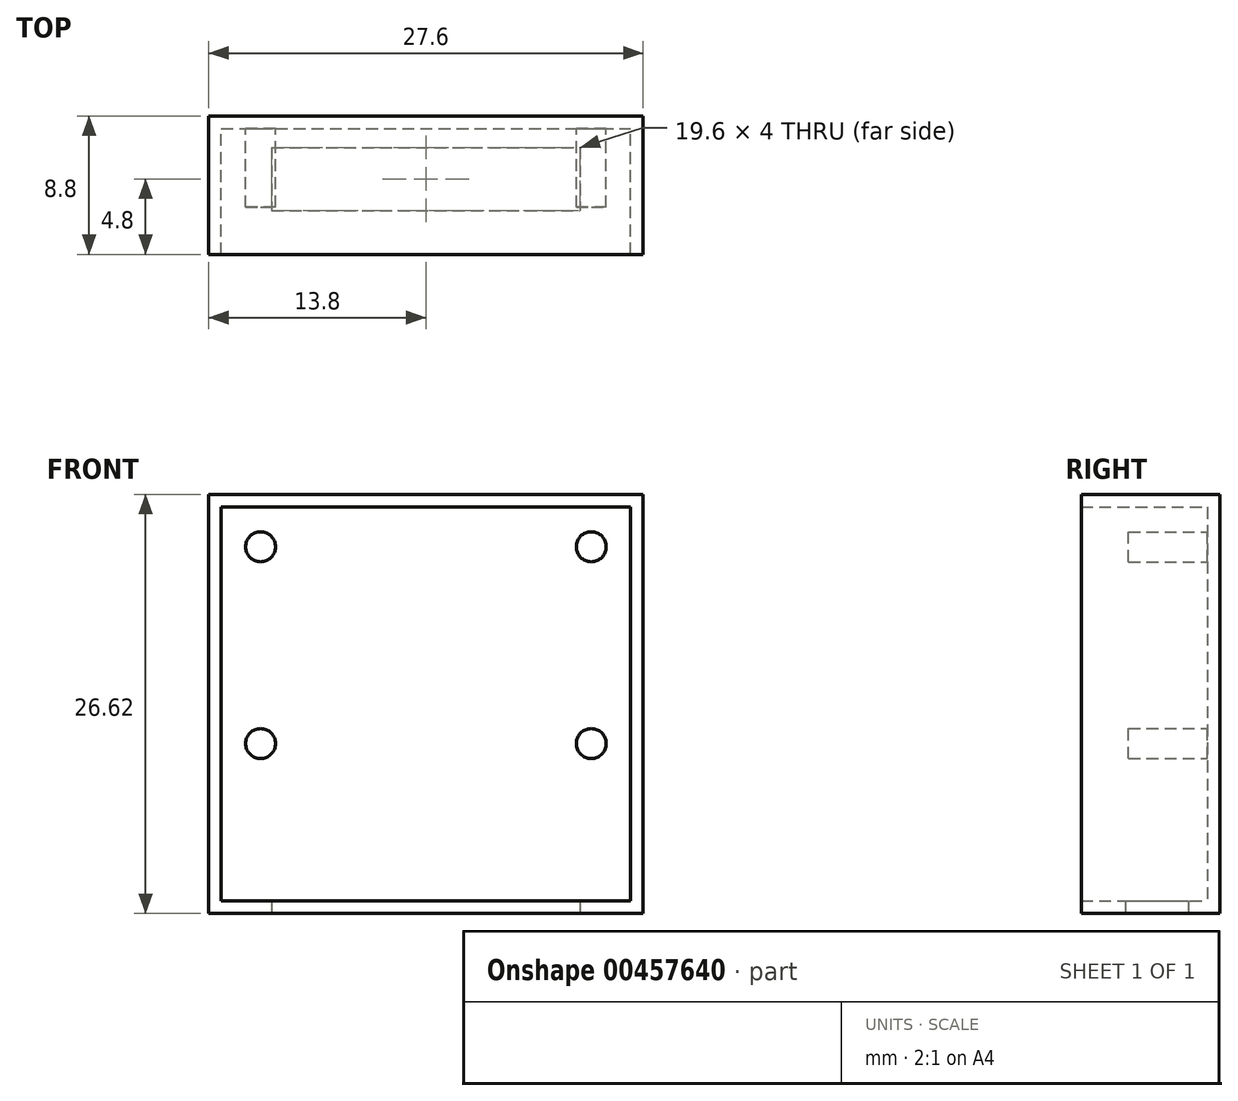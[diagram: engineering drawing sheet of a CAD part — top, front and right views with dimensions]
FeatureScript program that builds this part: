
annotation { "Feature Type Name" : "Feature", "Feature Type Description" : "" }
export const myFeature = defineFeature(function(context is Context, id is Id, definition is map)
    precondition{}
    {
        {
            var Q0;
            Q0=qCreatedBy(makeId("Front.planeOp"),FACE);
            var sketch = newSketch(context, id + "F0", { "sketchPlane" : qUnion([Q0])});
            skLineSegment(sketch, "E0.bottom", {"start": v(-12.5, 12) * mm, "end": v(12.5, 12) * mm, "construction": true});
            skLineSegment(sketch, "E0.top", {"start": v(-12.5, -12) * mm, "end": v(12.5, -12) * mm, "construction": true});
            skLineSegment(sketch, "E0.left", {"start": v(-12.5, 12) * mm, "end": v(-12.5, -12) * mm, "construction": true});
            skLineSegment(sketch, "E0.right", {"start": v(12.5, 12) * mm, "end": v(12.5, -12) * mm, "construction": true});
            skPoint(sketch, "E0.middle", {"position": v(0, 0) * mm});
            skLineSegment(sketch, "E1", {"start": v(0, 16.68) * mm, "end": v(0, -16.21) * mm, "construction": true});
            skPoint(sketch, "E1.endSnap0", {"position": v(0, -12) * mm});
            skLineSegment(sketch, "E2", {"start": v(-10.5, 14.1) * mm, "end": v(-10.5, -17.44) * mm, "construction": true});
            skLineSegment(sketch, "E3", {"start": v(-16.92, 10) * mm, "end": v(20.39, 10) * mm, "construction": true});
            skLineSegment(sketch, "E4", {"start": v(-17.84, -2.5) * mm, "end": v(19.35, -2.5) * mm, "construction": true});
            skCircle(sketch, "E5", {"center": v(-10.5, 10) * mm, "radius": 1 * mm, "construction": true});
            skCircle(sketch, "E6", {"center": v(-10.5, -2.5) * mm, "radius": 1 * mm, "construction": true});
            skCircle(sketch, "E7.MirrorC", {"center": v(10.5, 10) * mm, "radius": 1 * mm, "construction": true});
            skCircle(sketch, "E8.MirrorC", {"center": v(10.5, -2.5) * mm, "radius": 1 * mm, "construction": true});
            skCircle(sketch, "E9", {"center": v(0, -2.5) * mm, "radius": 4 * mm, "construction": true});
            skLineSegment(sketch, "E10.0", {"start": v(13, 12.51) * mm, "end": v(13, -12.51) * mm, "construction": true});
            skLineSegment(sketch, "E10.1", {"start": v(-13, 12.51) * mm, "end": v(13, 12.51) * mm, "construction": true});
            skLineSegment(sketch, "E10.2", {"start": v(-13, 12.5) * mm, "end": v(-13, -12.51) * mm, "construction": true});
            skLineSegment(sketch, "E10.3", {"start": v(-13, -12.51) * mm, "end": v(13, -12.51) * mm, "construction": true});
            skLineSegment(sketch, "E11.0", {"start": v(-13.8, 13.31) * mm, "end": v(13.8, 13.31) * mm});
            skLineSegment(sketch, "E11.1", {"start": v(-13.8, 13.31) * mm, "end": v(-13.8, -13.31) * mm});
            skLineSegment(sketch, "E11.2", {"start": v(-13.8, -13.31) * mm, "end": v(13.8, -13.31) * mm});
            skLineSegment(sketch, "E11.3", {"start": v(13.8, 13.31) * mm, "end": v(13.8, -13.31) * mm});
            skSolve(sketch);
        }
        {
            var Q0;
            Q0 = qSketchRegion(id + "F0", true);
            extrude(context, id + "F1", {"entities" : qUnion([Q0]), "depth" : .8 * mm});
        }
        {
            var Q0;
            Q0=makeQuery(id+"F1.opExtrude","CAP_FACE",FACE,{"disambiguationData":[OSD([sQuery(id+"F0.wireOp",EDGE,"E11.0"),sQuery(id+"F0.wireOp",EDGE,"E11.1"),sQuery(id+"F0.wireOp",EDGE,"E11.2"),sQuery(id+"F0.wireOp",EDGE,"E11.3")])],"isStart":false});
            var sketch = newSketch(context, id + "F2", { "sketchPlane" : qUnion([Q0])});
            skLineSegment(sketch, "E12.0", {"start": v(-13.8, 13.31) * mm, "end": v(13.8, 13.31) * mm});
            skLineSegment(sketch, "E13.0", {"start": v(-13, 12.51) * mm, "end": v(13, 12.51) * mm});
            skLineSegment(sketch, "E14.0", {"start": v(13.8, 13.31) * mm, "end": v(13.8, -13.31) * mm});
            skLineSegment(sketch, "E15.0", {"start": v(13, 12.51) * mm, "end": v(13, -12.51) * mm});
            skLineSegment(sketch, "E16.0", {"start": v(-13, -12.51) * mm, "end": v(13, -12.51) * mm});
            skLineSegment(sketch, "E17.0", {"start": v(-13.8, -13.31) * mm, "end": v(13.8, -13.31) * mm});
            skLineSegment(sketch, "E18.0", {"start": v(-13.8, 13.31) * mm, "end": v(-13.8, -13.31) * mm});
            skLineSegment(sketch, "E19.0", {"start": v(-13, 12.5) * mm, "end": v(-13, -12.51) * mm});
            skSolve(sketch);
        }
        {
            var Q0;
            Q0 = qSketchRegion(id + "F2", true);
            extrude(context, id + "F3", {"entities" : qUnion([Q0]), "operationType" : NewBodyOperationType.ADD, "depth" : 8 * mm});
        }
        {
            var Q0;
            Q0=makeQuery(id+"F1.opExtrude","CAP_FACE",FACE,{"disambiguationData":[OSD([sQuery(id+"F0.wireOp",EDGE,"E11.0"),sQuery(id+"F0.wireOp",EDGE,"E11.1"),sQuery(id+"F0.wireOp",EDGE,"E11.2"),sQuery(id+"F0.wireOp",EDGE,"E11.3")])],"isStart":false});
            var sketch = newSketch(context, id + "F4", { "sketchPlane" : qUnion([Q0])});
            skPoint(sketch, "E20.0", {"position": v(-10.5, 10) * mm});
            skCircle(sketch, "E21", {"center": v(-10.5, 10) * mm, "radius": 0.95 * mm});
            skCircle(sketch, "E22", {"center": v(-10.5, -2.5) * mm, "radius": 0.95 * mm});
            skCircle(sketch, "E23.MirrorC", {"center": v(10.5, 10) * mm, "radius": 0.95 * mm});
            skCircle(sketch, "E24.MirrorC", {"center": v(10.5, -2.5) * mm, "radius": 0.95 * mm});
            skSolve(sketch);
        }
        {
            var Q0;
            Q0 = qSketchRegion(id + "F4", true);
            extrude(context, id + "F5", {"entities" : qUnion([Q0]), "operationType" : NewBodyOperationType.ADD, "depth" : 5 * mm});
        }
        {
            var Q0;
            Q0=makeQuery(id+"F3.boolean.opBoolean","MERGE",FACE,{"derivedFrom":[makeQuery(id+"F1.opExtrude","SWEPT_FACE",FACE,{"disambiguationData":[OSD([sQuery(id+"F0.wireOp",EDGE,"E11.2")])]}),makeQuery(id+"F3.opExtrude","SWEPT_FACE",FACE,{"disambiguationData":[OSD([sQuery(id+"F2.wireOp",EDGE,"E17.0")])]})]});
            var sketch = newSketch(context, id + "F6", { "sketchPlane" : qUnion([Q0])});
            skLineSegment(sketch, "E25.bottom", {"start": v(-9.8, 2) * mm, "end": v(9.8, 2) * mm});
            skLineSegment(sketch, "E25.top", {"start": v(-9.8, 6) * mm, "end": v(9.8, 6) * mm});
            skLineSegment(sketch, "E25.left", {"start": v(-9.8, 2) * mm, "end": v(-9.8, 6) * mm});
            skLineSegment(sketch, "E25.right", {"start": v(9.8, 2) * mm, "end": v(9.8, 6) * mm});
            skSolve(sketch);
        }
        {
            var Q0;
            Q0 = qSketchRegion(id + "F6", true);
            extrude(context, id + "F7", {"entities" : qUnion([Q0]), "operationType" : NewBodyOperationType.REMOVE, "oppositeDirection" : true, "depth" : 1.7 * mm});
        }
    });
